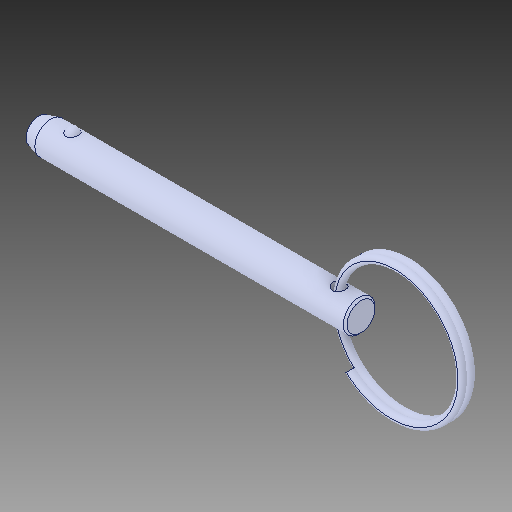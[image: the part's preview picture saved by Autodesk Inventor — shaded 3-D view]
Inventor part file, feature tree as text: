
AUTODESK INVENTOR PART (.ipt)
format: ipt  version: 2018 (Build 220112000, 112)  size: 299,520 bytes
history: native  units: in
note: dims shown in document units (in); Inventor stores cm internally (conversion verified against a paired STEP export)
features: revolve x1, other x1, sweep x1
ambient origin geometry x8: Origin, YZ Plane, XZ Plane, XY Plane, X Axis, Y Axis, Z Axis, Center Point
bodies: Solid1 (feature_tree), Solid2 (feature_tree), Solid3 (feature_tree)
feature tree (3):
  revolve  "Revolve2"  [1 undecoded]
  other  "Cut-Revolve2"
  sweep  "Sweep2"
note: 1 required parameter value undecoded (feature->parameter linkage not recoverable at this tier; creation-order binding heuristic only, values carry confidence <= 0.55)
